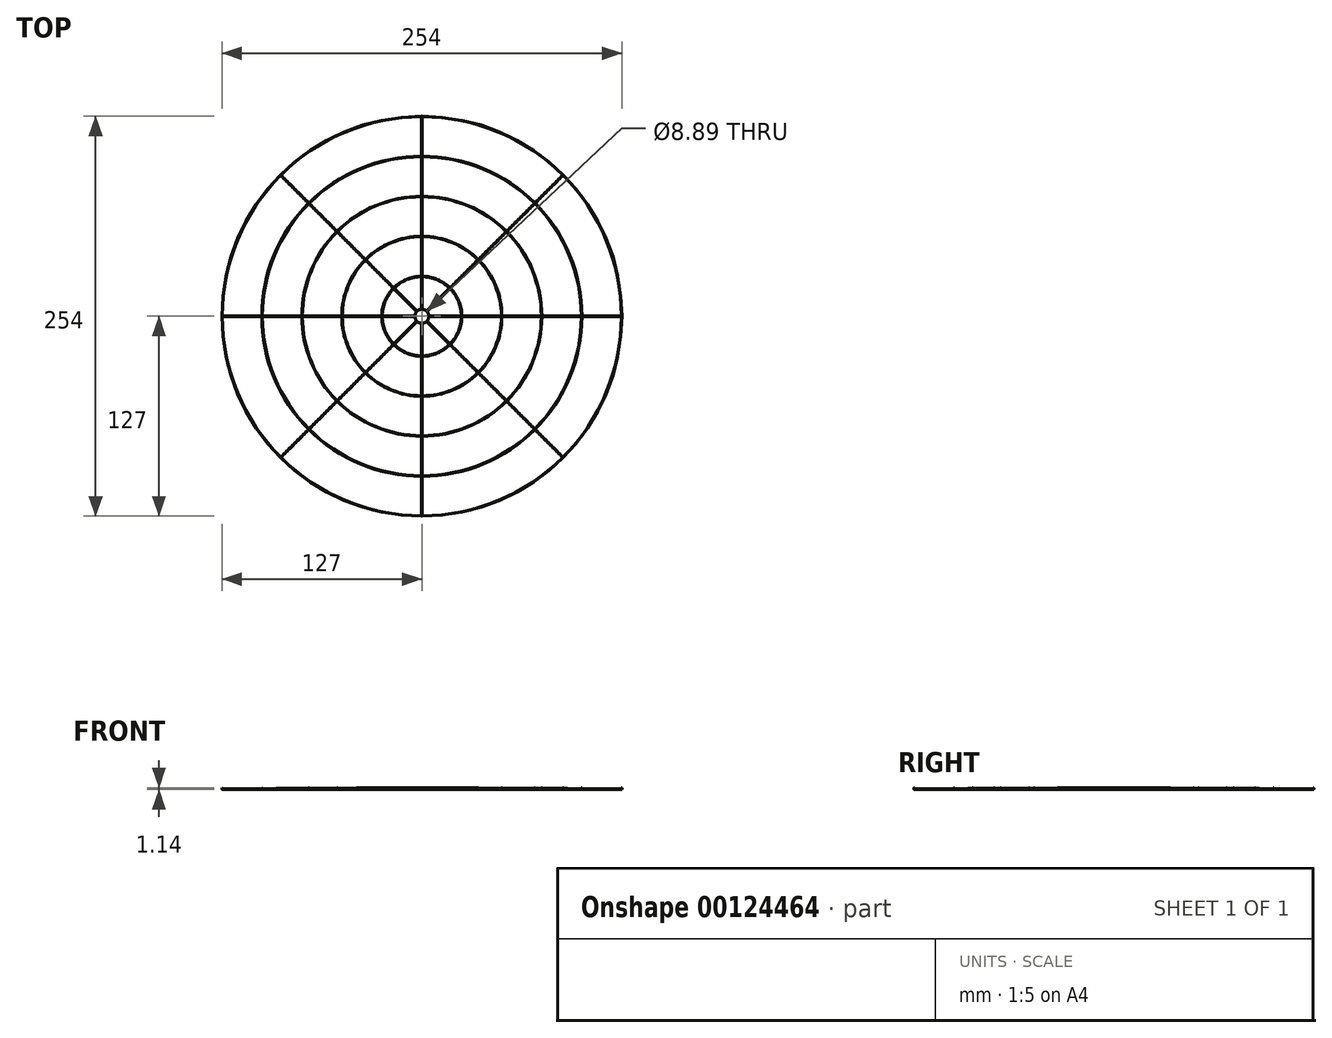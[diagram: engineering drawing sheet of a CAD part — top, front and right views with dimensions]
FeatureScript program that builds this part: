
annotation { "Feature Type Name" : "Feature", "Feature Type Description" : "" }
export const myFeature = defineFeature(function(context is Context, id is Id, definition is map)
    precondition{}
    {
        {
            var Q0;
            Q0=qCreatedBy(makeId("Front.planeOp"),FACE);
            var sketch = newSketch(context, id + "F0", { "sketchPlane" : qUnion([Q0])});
            skLineSegment(sketch, "E0", {"start": v(0, 0) * mm, "end": v(127, 0) * mm});
            skLineSegment(sketch, "E1", {"start": v(0, 0) * mm, "end": v(-127, 0) * mm});
            skLineSegment(sketch, "E2", {"start": v(-127, 0) * mm, "end": v(-127, 0.13) * mm});
            skLineSegment(sketch, "E3", {"start": v(0, 0) * mm, "end": v(0, 0.89) * mm});
            skLineSegment(sketch, "E4", {"start": v(0, 0.89) * mm, "end": v(-4.45, 0.89) * mm});
            skLineSegment(sketch, "E5", {"start": v(-4.45, 0.89) * mm, "end": v(-4.45, 0) * mm});
            skLineSegment(sketch, "E6.MirrorCS", {"start": v(0, 0.89) * mm, "end": v(4.45, 0.89) * mm});
            skLineSegment(sketch, "E7.MirrorCS", {"start": v(4.45, 0.89) * mm, "end": v(4.45, 0) * mm});
            skLineSegment(sketch, "E8.MirrorCS", {"start": v(127, 0) * mm, "end": v(127, 0.13) * mm});
            skLineSegment(sketch, "E9", {"start": v(127, 0.13) * mm, "end": v(4.45, 0.89) * mm});
            skLineSegment(sketch, "E10.MirrorCS", {"start": v(-127, 0.13) * mm, "end": v(-4.44, 0.89) * mm});
            skPoint(sketch, "E11", {"position": v(-127, 0.12) * mm});
            skPoint(sketch, "E12", {"position": v(-4.45, 0.89) * mm});
            skLineSegment(sketch, "E13", {"start": v(-4.44, 0.89) * mm, "end": v(-127, 0.12) * mm});
            skLineSegment(sketch, "E14.MirrorCS", {"start": v(4.45, 0.89) * mm, "end": v(127, 0.12) * mm});
            skSolve(sketch);
        }
        {
            var Q0;
            {var subQ0=sQuery(id+"F0.wireOp",EDGE,"E10.MirrorCS");Q0=makeQuery(id+"F0.imprint","IMPRINT",FACE,{"disambiguationData":[TD([[makeQuery(id+"F0.imprint","IMPRINT",EDGE,{"derivedFrom":subQ0}),-1.0]])]});}
            var Q1;
            Q1=sQuery(id+"F0.wireOp",EDGE,"E3");
            revolve(context, id + "F1", {"entities" : qUnion([Q0]), "axis" : qUnion([Q1]), "revolveType" : RevolveType.FULL});
        }
        {
            var Q0;
            Q0=qCreatedBy(makeId("Top.planeOp"),FACE);
            var sketch = newSketch(context, id + "F2", { "sketchPlane" : qUnion([Q0])});
            skCircle(sketch, "E15.0", {"center": v(0, 0) * mm, "radius": 127 * mm});
            skArc(sketch, "E16", {"start": v(-0.13, 76.2) * mm, "mid": v(-29.16, 70.4) * mm, "end": v(-53.8, 53.97) * mm});
            skArc(sketch, "E17", {"start": v(-0.13, 101.6) * mm, "mid": v(-38.88, 93.87) * mm, "end": v(-71.75, 71.93) * mm});
            skArc(sketch, "E18", {"start": v(-0.13, 50.8) * mm, "mid": v(-19.44, 46.93) * mm, "end": v(-35.83, 36.01) * mm});
            skArc(sketch, "E19", {"start": v(-0.13, 25.4) * mm, "mid": v(-9.72, 23.47) * mm, "end": v(-17.87, 18.05) * mm});
            skLineSegment(sketch, "E20", {"start": v(0, 0) * mm, "end": v(0, 4.45) * mm});
            skCircle(sketch, "E21.0", {"center": v(0, 0) * mm, "radius": 4.45 * mm});
            skLineSegment(sketch, "E22", {"start": v(-0.13, 5.62) * mm, "end": v(-0.13, 4.44) * mm});
            skLineSegment(sketch, "E23", {"start": v(0.13, 5.62) * mm, "end": v(0.13, 4.44) * mm});
            skLineSegment(sketch, "E24", {"start": v(-0.13, 5.62) * mm, "end": v(-0.13, 25.15) * mm});
            skLineSegment(sketch, "E25", {"start": v(0.13, 5.62) * mm, "end": v(0.13, 25.15) * mm});
            skLineSegment(sketch, "E26.1.0", {"start": v(-3.88, 4.06) * mm, "end": v(-17.7, 17.87) * mm});
            skLineSegment(sketch, "E26.1.1", {"start": v(-4.06, 3.88) * mm, "end": v(-17.87, 17.7) * mm});
            skLineSegment(sketch, "E26.1.2", {"start": v(-4.06, 3.88) * mm, "end": v(-3.23, 3.05) * mm});
            skLineSegment(sketch, "E26.1.3", {"start": v(-3.88, 4.06) * mm, "end": v(-3.05, 3.23) * mm});
            skLineSegment(sketch, "E26.2.0", {"start": v(-5.62, 0.13) * mm, "end": v(-25.15, 0.13) * mm});
            skLineSegment(sketch, "E26.2.1", {"start": v(-5.62, -0.13) * mm, "end": v(-25.15, -0.13) * mm});
            skLineSegment(sketch, "E26.2.2", {"start": v(-5.62, -0.13) * mm, "end": v(-4.44, -0.13) * mm});
            skLineSegment(sketch, "E26.2.3", {"start": v(-5.62, 0.13) * mm, "end": v(-4.44, 0.13) * mm});
            skLineSegment(sketch, "E26.3.0", {"start": v(-4.06, -3.88) * mm, "end": v(-17.87, -17.7) * mm});
            skLineSegment(sketch, "E26.3.1", {"start": v(-3.88, -4.06) * mm, "end": v(-17.7, -17.87) * mm});
            skLineSegment(sketch, "E26.3.2", {"start": v(-3.88, -4.06) * mm, "end": v(-3.05, -3.23) * mm});
            skLineSegment(sketch, "E26.3.3", {"start": v(-4.06, -3.88) * mm, "end": v(-3.23, -3.05) * mm});
            skLineSegment(sketch, "E26.4.0", {"start": v(-0.13, -5.62) * mm, "end": v(-0.13, -25.15) * mm});
            skLineSegment(sketch, "E26.4.1", {"start": v(0.13, -5.62) * mm, "end": v(0.13, -25.15) * mm});
            skLineSegment(sketch, "E26.4.2", {"start": v(0.13, -5.62) * mm, "end": v(0.13, -4.44) * mm});
            skLineSegment(sketch, "E26.4.3", {"start": v(-0.13, -5.62) * mm, "end": v(-0.13, -4.44) * mm});
            skLineSegment(sketch, "E26.5.0", {"start": v(3.88, -4.06) * mm, "end": v(17.7, -17.87) * mm});
            skLineSegment(sketch, "E26.5.1", {"start": v(4.06, -3.88) * mm, "end": v(17.87, -17.7) * mm});
            skLineSegment(sketch, "E26.5.2", {"start": v(4.06, -3.88) * mm, "end": v(3.23, -3.05) * mm});
            skLineSegment(sketch, "E26.5.3", {"start": v(3.88, -4.06) * mm, "end": v(3.05, -3.23) * mm});
            skLineSegment(sketch, "E26.6.0", {"start": v(5.62, -0.13) * mm, "end": v(25.15, -0.13) * mm});
            skLineSegment(sketch, "E26.6.1", {"start": v(5.62, 0.13) * mm, "end": v(25.15, 0.13) * mm});
            skLineSegment(sketch, "E26.6.2", {"start": v(5.62, 0.13) * mm, "end": v(4.44, 0.13) * mm});
            skLineSegment(sketch, "E26.6.3", {"start": v(5.62, -0.13) * mm, "end": v(4.44, -0.13) * mm});
            skLineSegment(sketch, "E26.7.0", {"start": v(4.06, 3.88) * mm, "end": v(17.87, 17.7) * mm});
            skLineSegment(sketch, "E26.7.1", {"start": v(3.88, 4.06) * mm, "end": v(17.7, 17.87) * mm});
            skLineSegment(sketch, "E26.7.2", {"start": v(3.88, 4.06) * mm, "end": v(3.05, 3.23) * mm});
            skLineSegment(sketch, "E26.7.3", {"start": v(4.06, 3.88) * mm, "end": v(3.23, 3.05) * mm});
            skArc(sketch, "E27.trimOffspring", {"start": v(17.87, 18.05) * mm, "mid": v(9.72, 23.47) * mm, "end": v(0.13, 25.4) * mm});
            skArc(sketch, "E28.trimOffspring", {"start": v(35.83, 36.01) * mm, "mid": v(19.44, 46.93) * mm, "end": v(0.13, 50.8) * mm});
            skArc(sketch, "E29.trimOffspring", {"start": v(53.8, 53.97) * mm, "mid": v(29.16, 70.4) * mm, "end": v(0.13, 76.2) * mm});
            skArc(sketch, "E30.trimOffspring", {"start": v(71.75, 71.93) * mm, "mid": v(38.88, 93.87) * mm, "end": v(0.13, 101.6) * mm});
            skArc(sketch, "E31.trimOffspring", {"start": v(101.6, 0.13) * mm, "mid": v(93.87, 38.88) * mm, "end": v(71.93, 71.75) * mm});
            skArc(sketch, "E32.trimOffspring", {"start": v(76.2, 0.13) * mm, "mid": v(70.4, 29.16) * mm, "end": v(53.97, 53.8) * mm});
            skArc(sketch, "E33.trimOffspring", {"start": v(50.8, 0.13) * mm, "mid": v(46.93, 19.44) * mm, "end": v(36.01, 35.83) * mm});
            skArc(sketch, "E34.trimOffspring", {"start": v(25.4, 0.13) * mm, "mid": v(23.47, 9.72) * mm, "end": v(18.05, 17.87) * mm});
            skArc(sketch, "E35.trimOffspring", {"start": v(18.05, -17.87) * mm, "mid": v(23.47, -9.72) * mm, "end": v(25.4, -0.13) * mm});
            skArc(sketch, "E36.trimOffspring", {"start": v(36.01, -35.83) * mm, "mid": v(46.93, -19.44) * mm, "end": v(50.8, -0.13) * mm});
            skArc(sketch, "E37.trimOffspring", {"start": v(53.97, -53.8) * mm, "mid": v(70.4, -29.16) * mm, "end": v(76.2, -0.13) * mm});
            skArc(sketch, "E38.trimOffspring", {"start": v(71.93, -71.75) * mm, "mid": v(93.87, -38.88) * mm, "end": v(101.6, -0.13) * mm});
            skArc(sketch, "E39.trimOffspring", {"start": v(0.13, -101.6) * mm, "mid": v(38.88, -93.87) * mm, "end": v(71.75, -71.93) * mm});
            skArc(sketch, "E40.trimOffspring", {"start": v(0.13, -76.2) * mm, "mid": v(29.16, -70.4) * mm, "end": v(53.8, -53.97) * mm});
            skArc(sketch, "E41.trimOffspring", {"start": v(0.13, -50.8) * mm, "mid": v(19.44, -46.93) * mm, "end": v(35.83, -36.01) * mm});
            skArc(sketch, "E42.trimOffspring", {"start": v(0.13, -25.4) * mm, "mid": v(9.72, -23.47) * mm, "end": v(17.87, -18.05) * mm});
            skArc(sketch, "E43.trimOffspring", {"start": v(-17.87, -18.05) * mm, "mid": v(-9.72, -23.47) * mm, "end": v(-0.13, -25.4) * mm});
            skArc(sketch, "E44.trimOffspring", {"start": v(-35.83, -36.01) * mm, "mid": v(-19.44, -46.93) * mm, "end": v(-0.13, -50.8) * mm});
            skArc(sketch, "E45.trimOffspring", {"start": v(-53.8, -53.97) * mm, "mid": v(-29.16, -70.4) * mm, "end": v(-0.13, -76.2) * mm});
            skArc(sketch, "E46.trimOffspring", {"start": v(-71.75, -71.93) * mm, "mid": v(-38.88, -93.87) * mm, "end": v(-0.13, -101.6) * mm});
            skArc(sketch, "E47.trimOffspring", {"start": v(-50.8, -0.13) * mm, "mid": v(-46.93, -19.44) * mm, "end": v(-36.01, -35.83) * mm});
            skArc(sketch, "E48.trimOffspring", {"start": v(-25.4, -0.13) * mm, "mid": v(-23.47, -9.72) * mm, "end": v(-18.05, -17.87) * mm});
            skArc(sketch, "E49.trimOffspring", {"start": v(-76.2, -0.13) * mm, "mid": v(-70.4, -29.16) * mm, "end": v(-53.97, -53.8) * mm});
            skArc(sketch, "E50.trimOffspring", {"start": v(-101.6, -0.13) * mm, "mid": v(-93.87, -38.88) * mm, "end": v(-71.93, -71.75) * mm});
            skArc(sketch, "E51.trimOffspring", {"start": v(-18.05, 17.87) * mm, "mid": v(-23.47, 9.72) * mm, "end": v(-25.4, 0.13) * mm});
            skArc(sketch, "E52.trimOffspring", {"start": v(-36.01, 35.83) * mm, "mid": v(-46.93, 19.44) * mm, "end": v(-50.8, 0.13) * mm});
            skArc(sketch, "E53.trimOffspring", {"start": v(-53.97, 53.8) * mm, "mid": v(-70.4, 29.16) * mm, "end": v(-76.2, 0.13) * mm});
            skArc(sketch, "E54.trimOffspring", {"start": v(-71.93, 71.75) * mm, "mid": v(-93.87, 38.88) * mm, "end": v(-101.6, 0.13) * mm});
            skArc(sketch, "E55", {"start": v(-89.71, 89.53) * mm, "mid": v(-117.1, 48.5) * mm, "end": v(-126.75, 0.13) * mm});
            skArc(sketch, "E56.trimOffspring", {"start": v(-0.13, 126.75) * mm, "mid": v(-48.5, 117.1) * mm, "end": v(-89.53, 89.71) * mm});
            skArc(sketch, "E57.trimOffspring", {"start": v(89.53, 89.71) * mm, "mid": v(48.5, 117.1) * mm, "end": v(0.13, 126.75) * mm});
            skArc(sketch, "E58.trimOffspring", {"start": v(126.75, 0.13) * mm, "mid": v(117.1, 48.5) * mm, "end": v(89.71, 89.53) * mm});
            skArc(sketch, "E59.trimOffspring", {"start": v(89.71, -89.53) * mm, "mid": v(117.1, -48.5) * mm, "end": v(126.75, -0.13) * mm});
            skArc(sketch, "E60.trimOffspring", {"start": v(0.13, -126.75) * mm, "mid": v(48.5, -117.1) * mm, "end": v(89.53, -89.71) * mm});
            skArc(sketch, "E61.trimOffspring", {"start": v(-89.53, -89.71) * mm, "mid": v(-48.5, -117.1) * mm, "end": v(-0.13, -126.75) * mm});
            skArc(sketch, "E62.trimOffspring", {"start": v(-126.75, -0.13) * mm, "mid": v(-117.1, -48.5) * mm, "end": v(-89.71, -89.53) * mm});
            skPoint(sketch, "E63.orphan", {"position": v(-89.9, 89.71) * mm});
            skPoint(sketch, "E64.orphan", {"position": v(-89.71, 89.9) * mm});
            skPoint(sketch, "E65.orphan", {"position": v(-0.13, 127) * mm});
            skPoint(sketch, "E66.orphan", {"position": v(0.13, 127) * mm});
            skPoint(sketch, "E67.orphan", {"position": v(89.71, 89.9) * mm});
            skPoint(sketch, "E68.orphan", {"position": v(89.9, 89.71) * mm});
            skPoint(sketch, "E69.orphan", {"position": v(127, 0.13) * mm});
            skPoint(sketch, "E70.orphan", {"position": v(127, -0.13) * mm});
            skPoint(sketch, "E71.orphan", {"position": v(89.71, -89.9) * mm});
            skPoint(sketch, "E72.orphan", {"position": v(89.9, -89.71) * mm});
            skPoint(sketch, "E73.orphan", {"position": v(-0.13, -127) * mm});
            skPoint(sketch, "E74.orphan", {"position": v(0.13, -127) * mm});
            skPoint(sketch, "E75.orphan", {"position": v(-89.9, -89.71) * mm});
            skPoint(sketch, "E76.orphan", {"position": v(-89.71, -89.9) * mm});
            skPoint(sketch, "E77.orphan", {"position": v(-127, 0.13) * mm});
            skPoint(sketch, "E78.orphan", {"position": v(-127, -0.13) * mm});
            skArc(sketch, "E79", {"start": v(-0.13, 101.35) * mm, "mid": v(-38.78, 93.63) * mm, "end": v(-71.57, 71.75) * mm});
            skLineSegment(sketch, "E80.trimOffspring", {"start": v(-0.13, 101.6) * mm, "end": v(-0.13, 126.75) * mm});
            skLineSegment(sketch, "E81.trimOffspring", {"start": v(0.13, 101.6) * mm, "end": v(0.13, 126.75) * mm});
            skArc(sketch, "E82.trimOffspring", {"start": v(71.57, 71.75) * mm, "mid": v(38.78, 93.63) * mm, "end": v(0.13, 101.35) * mm});
            skLineSegment(sketch, "E83.trimOffspring", {"start": v(71.75, 71.93) * mm, "end": v(89.53, 89.71) * mm});
            skLineSegment(sketch, "E84.trimOffspring", {"start": v(71.93, 71.75) * mm, "end": v(89.71, 89.53) * mm});
            skLineSegment(sketch, "E85.trimOffspring", {"start": v(101.6, 0.13) * mm, "end": v(126.75, 0.13) * mm});
            skArc(sketch, "E86.trimOffspring", {"start": v(101.35, 0.13) * mm, "mid": v(93.63, 38.78) * mm, "end": v(71.75, 71.57) * mm});
            skLineSegment(sketch, "E87.trimOffspring", {"start": v(101.6, -0.13) * mm, "end": v(126.75, -0.13) * mm});
            skLineSegment(sketch, "E88.trimOffspring", {"start": v(71.93, -71.75) * mm, "end": v(89.71, -89.53) * mm});
            skArc(sketch, "E89.trimOffspring", {"start": v(71.75, -71.57) * mm, "mid": v(93.63, -38.78) * mm, "end": v(101.35, -0.13) * mm});
            skLineSegment(sketch, "E90.trimOffspring", {"start": v(71.75, -71.93) * mm, "end": v(89.53, -89.71) * mm});
            skLineSegment(sketch, "E91.trimOffspring", {"start": v(0.13, -101.6) * mm, "end": v(0.13, -126.75) * mm});
            skLineSegment(sketch, "E92.trimOffspring", {"start": v(-0.13, -101.6) * mm, "end": v(-0.13, -126.75) * mm});
            skArc(sketch, "E93.trimOffspring", {"start": v(0.13, -101.35) * mm, "mid": v(38.78, -93.63) * mm, "end": v(71.57, -71.75) * mm});
            skLineSegment(sketch, "E94.trimOffspring", {"start": v(-71.93, -71.75) * mm, "end": v(-89.71, -89.53) * mm});
            skArc(sketch, "E95.trimOffspring", {"start": v(-71.57, -71.75) * mm, "mid": v(-38.78, -93.63) * mm, "end": v(-0.13, -101.35) * mm});
            skLineSegment(sketch, "E96.trimOffspring", {"start": v(-71.75, -71.93) * mm, "end": v(-89.53, -89.71) * mm});
            skArc(sketch, "E97.trimOffspring", {"start": v(-101.35, -0.13) * mm, "mid": v(-93.63, -38.78) * mm, "end": v(-71.75, -71.57) * mm});
            skLineSegment(sketch, "E98.trimOffspring", {"start": v(-101.6, 0.13) * mm, "end": v(-126.75, 0.13) * mm});
            skLineSegment(sketch, "E99.trimOffspring", {"start": v(-101.6, -0.13) * mm, "end": v(-126.75, -0.13) * mm});
            skLineSegment(sketch, "E100.trimOffspring", {"start": v(-71.75, 71.93) * mm, "end": v(-89.53, 89.71) * mm});
            skLineSegment(sketch, "E101.trimOffspring", {"start": v(-71.93, 71.75) * mm, "end": v(-89.71, 89.53) * mm});
            skArc(sketch, "E102.trimOffspring", {"start": v(-71.75, 71.57) * mm, "mid": v(-93.63, 38.78) * mm, "end": v(-101.35, 0.13) * mm});
            skArc(sketch, "E103", {"start": v(-0.13, 75.95) * mm, "mid": v(-29.06, 70.16) * mm, "end": v(-53.61, 53.8) * mm});
            skLineSegment(sketch, "E104.trimOffspring", {"start": v(-0.13, 76.2) * mm, "end": v(-0.13, 101.35) * mm});
            skLineSegment(sketch, "E105.trimOffspring", {"start": v(0.13, 76.2) * mm, "end": v(0.13, 101.35) * mm});
            skArc(sketch, "E106.trimOffspring", {"start": v(53.61, 53.8) * mm, "mid": v(29.06, 70.16) * mm, "end": v(0.13, 75.95) * mm});
            skLineSegment(sketch, "E107.trimOffspring", {"start": v(53.8, 53.97) * mm, "end": v(71.57, 71.75) * mm});
            skLineSegment(sketch, "E108.trimOffspring", {"start": v(53.97, 53.8) * mm, "end": v(71.75, 71.57) * mm});
            skArc(sketch, "E109.trimOffspring", {"start": v(75.95, 0.13) * mm, "mid": v(70.16, 29.06) * mm, "end": v(53.8, 53.61) * mm});
            skLineSegment(sketch, "E110.trimOffspring", {"start": v(76.2, 0.13) * mm, "end": v(101.35, 0.13) * mm});
            skLineSegment(sketch, "E111.trimOffspring", {"start": v(76.2, -0.13) * mm, "end": v(101.35, -0.13) * mm});
            skArc(sketch, "E112.trimOffspring", {"start": v(53.8, -53.61) * mm, "mid": v(70.16, -29.06) * mm, "end": v(75.95, -0.13) * mm});
            skLineSegment(sketch, "E113.trimOffspring", {"start": v(53.97, -53.8) * mm, "end": v(71.75, -71.57) * mm});
            skLineSegment(sketch, "E114.trimOffspring", {"start": v(53.8, -53.97) * mm, "end": v(71.57, -71.75) * mm});
            skArc(sketch, "E115.trimOffspring", {"start": v(0.13, -75.95) * mm, "mid": v(29.06, -70.16) * mm, "end": v(53.61, -53.8) * mm});
            skLineSegment(sketch, "E116.trimOffspring", {"start": v(-0.13, -76.2) * mm, "end": v(-0.13, -101.35) * mm});
            skLineSegment(sketch, "E117.trimOffspring", {"start": v(0.13, -76.2) * mm, "end": v(0.13, -101.35) * mm});
            skArc(sketch, "E118.trimOffspring", {"start": v(-53.61, -53.8) * mm, "mid": v(-29.06, -70.16) * mm, "end": v(-0.13, -75.95) * mm});
            skLineSegment(sketch, "E119.trimOffspring", {"start": v(-53.97, -53.8) * mm, "end": v(-71.75, -71.57) * mm});
            skLineSegment(sketch, "E120.trimOffspring", {"start": v(-53.8, -53.97) * mm, "end": v(-71.57, -71.75) * mm});
            skLineSegment(sketch, "E121.trimOffspring", {"start": v(-76.2, 0.13) * mm, "end": v(-101.35, 0.13) * mm});
            skLineSegment(sketch, "E122.trimOffspring", {"start": v(-76.2, -0.13) * mm, "end": v(-101.35, -0.13) * mm});
            skArc(sketch, "E123.trimOffspring", {"start": v(-75.95, -0.13) * mm, "mid": v(-70.16, -29.06) * mm, "end": v(-53.8, -53.61) * mm});
            skLineSegment(sketch, "E124.trimOffspring", {"start": v(-53.97, 53.8) * mm, "end": v(-71.75, 71.57) * mm});
            skArc(sketch, "E125.trimOffspring", {"start": v(-53.8, 53.61) * mm, "mid": v(-70.16, 29.06) * mm, "end": v(-75.95, 0.13) * mm});
            skLineSegment(sketch, "E126.trimOffspring", {"start": v(-53.8, 53.97) * mm, "end": v(-71.57, 71.75) * mm});
            skArc(sketch, "E127", {"start": v(-0.13, 50.55) * mm, "mid": v(-19.34, 46.7) * mm, "end": v(-35.65, 35.83) * mm});
            skLineSegment(sketch, "E128.trimOffspring", {"start": v(-0.13, 50.8) * mm, "end": v(-0.13, 75.95) * mm});
            skLineSegment(sketch, "E129.trimOffspring", {"start": v(0.13, 50.8) * mm, "end": v(0.13, 75.95) * mm});
            skLineSegment(sketch, "E130.trimOffspring", {"start": v(35.83, 36.01) * mm, "end": v(53.61, 53.8) * mm});
            skArc(sketch, "E131.trimOffspring", {"start": v(35.65, 35.83) * mm, "mid": v(19.34, 46.7) * mm, "end": v(0.13, 50.55) * mm});
            skLineSegment(sketch, "E132.trimOffspring", {"start": v(36.01, 35.83) * mm, "end": v(53.8, 53.61) * mm});
            skLineSegment(sketch, "E133.trimOffspring", {"start": v(50.8, 0.13) * mm, "end": v(75.95, 0.13) * mm});
            skLineSegment(sketch, "E134.trimOffspring", {"start": v(50.8, -0.13) * mm, "end": v(75.95, -0.13) * mm});
            skArc(sketch, "E135.trimOffspring", {"start": v(50.55, 0.13) * mm, "mid": v(46.7, 19.34) * mm, "end": v(35.83, 35.65) * mm});
            skArc(sketch, "E136.trimOffspring", {"start": v(35.83, -35.65) * mm, "mid": v(46.7, -19.34) * mm, "end": v(50.55, -0.13) * mm});
            skLineSegment(sketch, "E137.trimOffspring", {"start": v(36.01, -35.83) * mm, "end": v(53.8, -53.61) * mm});
            skLineSegment(sketch, "E138.trimOffspring", {"start": v(35.83, -36.01) * mm, "end": v(53.61, -53.8) * mm});
            skArc(sketch, "E139.trimOffspring", {"start": v(0.13, -50.55) * mm, "mid": v(19.34, -46.7) * mm, "end": v(35.65, -35.83) * mm});
            skLineSegment(sketch, "E140.trimOffspring", {"start": v(-0.13, -50.8) * mm, "end": v(-0.13, -75.95) * mm});
            skLineSegment(sketch, "E141.trimOffspring", {"start": v(0.13, -50.8) * mm, "end": v(0.13, -75.95) * mm});
            skLineSegment(sketch, "E142.trimOffspring", {"start": v(-36.01, -35.83) * mm, "end": v(-53.8, -53.61) * mm});
            skArc(sketch, "E143.trimOffspring", {"start": v(-35.65, -35.83) * mm, "mid": v(-19.34, -46.7) * mm, "end": v(-0.13, -50.55) * mm});
            skLineSegment(sketch, "E144.trimOffspring", {"start": v(-35.83, -36.01) * mm, "end": v(-53.61, -53.8) * mm});
            skLineSegment(sketch, "E145.trimOffspring", {"start": v(-50.8, 0.13) * mm, "end": v(-75.95, 0.13) * mm});
            skLineSegment(sketch, "E146.trimOffspring", {"start": v(-50.8, -0.13) * mm, "end": v(-75.95, -0.13) * mm});
            skLineSegment(sketch, "E147.trimOffspring", {"start": v(-35.83, 36.01) * mm, "end": v(-53.61, 53.8) * mm});
            skLineSegment(sketch, "E148.trimOffspring", {"start": v(-36.01, 35.83) * mm, "end": v(-53.8, 53.61) * mm});
            skArc(sketch, "E149.trimOffspring", {"start": v(-35.83, 35.65) * mm, "mid": v(-50.55, 0) * mm, "end": v(-35.83, -35.65) * mm});
            skArc(sketch, "E150", {"start": v(-0.13, 25.15) * mm, "mid": v(-9.62, 23.23) * mm, "end": v(-17.7, 17.87) * mm});
            skLineSegment(sketch, "E151.trimOffspring", {"start": v(-0.13, 25.4) * mm, "end": v(-0.13, 50.55) * mm});
            skLineSegment(sketch, "E152.trimOffspring", {"start": v(0.13, 25.4) * mm, "end": v(0.13, 50.55) * mm});
            skLineSegment(sketch, "E153.trimOffspring", {"start": v(17.87, 18.05) * mm, "end": v(35.65, 35.83) * mm});
            skArc(sketch, "E154.trimOffspring", {"start": v(17.7, 17.87) * mm, "mid": v(9.62, 23.23) * mm, "end": v(0.13, 25.15) * mm});
            skLineSegment(sketch, "E155.trimOffspring", {"start": v(18.05, 17.87) * mm, "end": v(35.83, 35.65) * mm});
            skLineSegment(sketch, "E156.trimOffspring", {"start": v(25.4, -0.13) * mm, "end": v(50.55, -0.13) * mm});
            skArc(sketch, "E157.trimOffspring", {"start": v(25.15, 0.13) * mm, "mid": v(23.23, 9.62) * mm, "end": v(17.87, 17.7) * mm});
            skLineSegment(sketch, "E158.trimOffspring", {"start": v(25.4, 0.13) * mm, "end": v(50.55, 0.13) * mm});
            skLineSegment(sketch, "E159.trimOffspring", {"start": v(17.87, -18.05) * mm, "end": v(35.65, -35.83) * mm});
            skArc(sketch, "E160.trimOffspring", {"start": v(17.87, -17.7) * mm, "mid": v(23.23, -9.62) * mm, "end": v(25.15, -0.13) * mm});
            skLineSegment(sketch, "E161.trimOffspring", {"start": v(18.05, -17.87) * mm, "end": v(35.83, -35.65) * mm});
            skArc(sketch, "E162.trimOffspring", {"start": v(0.13, -25.15) * mm, "mid": v(9.62, -23.23) * mm, "end": v(17.7, -17.87) * mm});
            skLineSegment(sketch, "E163.trimOffspring", {"start": v(-0.13, -25.4) * mm, "end": v(-0.13, -50.55) * mm});
            skLineSegment(sketch, "E164.trimOffspring", {"start": v(0.13, -25.4) * mm, "end": v(0.13, -50.55) * mm});
            skLineSegment(sketch, "E165.trimOffspring", {"start": v(-18.05, -17.87) * mm, "end": v(-35.83, -35.65) * mm});
            skLineSegment(sketch, "E166.trimOffspring", {"start": v(-17.87, -18.05) * mm, "end": v(-35.65, -35.83) * mm});
            skArc(sketch, "E167.trimOffspring", {"start": v(-17.7, -17.87) * mm, "mid": v(-9.62, -23.23) * mm, "end": v(-0.13, -25.15) * mm});
            skArc(sketch, "E168.trimOffspring", {"start": v(-25.15, -0.13) * mm, "mid": v(-23.23, -9.62) * mm, "end": v(-17.87, -17.7) * mm});
            skLineSegment(sketch, "E169.trimOffspring", {"start": v(-25.4, 0.13) * mm, "end": v(-50.55, 0.13) * mm});
            skLineSegment(sketch, "E170.trimOffspring", {"start": v(-25.4, -0.13) * mm, "end": v(-50.55, -0.13) * mm});
            skArc(sketch, "E171.trimOffspring", {"start": v(-17.87, 17.7) * mm, "mid": v(-23.23, 9.62) * mm, "end": v(-25.15, 0.13) * mm});
            skLineSegment(sketch, "E172.trimOffspring", {"start": v(-18.05, 17.87) * mm, "end": v(-35.83, 35.65) * mm});
            skLineSegment(sketch, "E173.trimOffspring", {"start": v(-17.87, 18.05) * mm, "end": v(-35.65, 35.83) * mm});
            skSolve(sketch);
        }
        {
            var Q0;
            Q0=makeQuery(id+"F2.imprint","IMPRINT",FACE,{"disambiguationData":[TD([[makeQuery(id+"F2.imprint","IMPRINT",EDGE,{"derivedFrom":sQuery(id+"F2.wireOp",EDGE,"E15.0")}),1.0]])]});
            extrude(context, id + "F3", {"entities" : qUnion([Q0]), "operationType" : NewBodyOperationType.REMOVE, "depth" : 25.4 * mm});
        }
        {
            var Q0;
            {var subQ0=sQuery(id+"F0.wireOp",EDGE,"E10.MirrorCS");Q0=makeQuery(id+"F0.imprint","IMPRINT",FACE,{"disambiguationData":[TD([[makeQuery(id+"F0.imprint","IMPRINT",EDGE,{"derivedFrom":subQ0}),-1.0]])]});}
            var Q1;
            Q1=sQuery(id+"F0.wireOp",EDGE,"E3");
            revolve(context, id + "F4", {"entities" : qUnion([Q0]), "axis" : qUnion([Q1]), "revolveType" : RevolveType.FULL});
        }
        {
            var Q0;
            Q0=makeQuery(id+"F2.imprint","IMPRINT",FACE,{"disambiguationData":[TD([[makeQuery(id+"F2.imprint","IMPRINT",EDGE,{"derivedFrom":sQuery(id+"F2.wireOp",EDGE,"E46.trimOffspring")}),-1.0]])]});
            var Q1;
            Q1=makeQuery(id+"F2.imprint","IMPRINT",FACE,{"disambiguationData":[TD([[makeQuery(id+"F2.imprint","IMPRINT",EDGE,{"derivedFrom":sQuery(id+"F2.wireOp",EDGE,"E45.trimOffspring")}),-1.0]])]});
            var Q2;
            Q2=makeQuery(id+"F2.imprint","IMPRINT",FACE,{"disambiguationData":[TD([[makeQuery(id+"F2.imprint","IMPRINT",EDGE,{"derivedFrom":sQuery(id+"F2.wireOp",EDGE,"E50.trimOffspring")}),-1.0]])]});
            var Q3;
            Q3=makeQuery(id+"F2.imprint","IMPRINT",FACE,{"disambiguationData":[TD([[makeQuery(id+"F2.imprint","IMPRINT",EDGE,{"derivedFrom":sQuery(id+"F2.wireOp",EDGE,"E49.trimOffspring")}),-1.0]])]});
            var Q4;
            Q4=makeQuery(id+"F2.imprint","IMPRINT",FACE,{"disambiguationData":[TD([[makeQuery(id+"F2.imprint","IMPRINT",EDGE,{"derivedFrom":sQuery(id+"F2.wireOp",EDGE,"E54.trimOffspring")}),-1.0]])]});
            var Q5;
            Q5=makeQuery(id+"F2.imprint","IMPRINT",FACE,{"disambiguationData":[TD([[makeQuery(id+"F2.imprint","IMPRINT",EDGE,{"derivedFrom":sQuery(id+"F2.wireOp",EDGE,"E53.trimOffspring")}),-1.0]])]});
            var Q6;
            Q6=makeQuery(id+"F2.imprint","IMPRINT",FACE,{"disambiguationData":[TD([[makeQuery(id+"F2.imprint","IMPRINT",EDGE,{"derivedFrom":sQuery(id+"F2.wireOp",EDGE,"E52.trimOffspring")}),-1.0]])]});
            var Q7;
            Q7=makeQuery(id+"F2.imprint","IMPRINT",FACE,{"disambiguationData":[TD([[makeQuery(id+"F2.imprint","IMPRINT",EDGE,{"derivedFrom":sQuery(id+"F2.wireOp",EDGE,"E48.trimOffspring")}),-1.0]])]});
            var Q8;
            Q8=makeQuery(id+"F2.imprint","IMPRINT",FACE,{"disambiguationData":[TD([[makeQuery(id+"F2.imprint","IMPRINT",EDGE,{"derivedFrom":sQuery(id+"F2.wireOp",EDGE,"E44.trimOffspring")}),-1.0]])]});
            var Q9;
            Q9=makeQuery(id+"F2.imprint","IMPRINT",FACE,{"disambiguationData":[TD([[makeQuery(id+"F2.imprint","IMPRINT",EDGE,{"derivedFrom":sQuery(id+"F2.wireOp",EDGE,"E41.trimOffspring")}),-1.0]])]});
            var Q10;
            Q10=makeQuery(id+"F2.imprint","IMPRINT",FACE,{"disambiguationData":[TD([[makeQuery(id+"F2.imprint","IMPRINT",EDGE,{"derivedFrom":sQuery(id+"F2.wireOp",EDGE,"E40.trimOffspring")}),-1.0]])]});
            var Q11;
            Q11=makeQuery(id+"F2.imprint","IMPRINT",FACE,{"disambiguationData":[TD([[makeQuery(id+"F2.imprint","IMPRINT",EDGE,{"derivedFrom":sQuery(id+"F2.wireOp",EDGE,"E39.trimOffspring")}),-1.0]])]});
            var Q12;
            Q12=makeQuery(id+"F2.imprint","IMPRINT",FACE,{"disambiguationData":[TD([[makeQuery(id+"F2.imprint","IMPRINT",EDGE,{"derivedFrom":sQuery(id+"F2.wireOp",EDGE,"E38.trimOffspring")}),-1.0]])]});
            var Q13;
            Q13=makeQuery(id+"F2.imprint","IMPRINT",FACE,{"disambiguationData":[TD([[makeQuery(id+"F2.imprint","IMPRINT",EDGE,{"derivedFrom":sQuery(id+"F2.wireOp",EDGE,"E37.trimOffspring")}),-1.0]])]});
            var Q14;
            Q14=makeQuery(id+"F2.imprint","IMPRINT",FACE,{"disambiguationData":[TD([[makeQuery(id+"F2.imprint","IMPRINT",EDGE,{"derivedFrom":sQuery(id+"F2.wireOp",EDGE,"E36.trimOffspring")}),-1.0]])]});
            var Q15;
            Q15=makeQuery(id+"F2.imprint","IMPRINT",FACE,{"disambiguationData":[TD([[makeQuery(id+"F2.imprint","IMPRINT",EDGE,{"derivedFrom":sQuery(id+"F2.wireOp",EDGE,"E35.trimOffspring")}),-1.0]])]});
            var Q16;
            Q16=makeQuery(id+"F2.imprint","IMPRINT",FACE,{"disambiguationData":[TD([[makeQuery(id+"F2.imprint","IMPRINT",EDGE,{"derivedFrom":sQuery(id+"F2.wireOp",EDGE,"E42.trimOffspring")}),-1.0]])]});
            var Q17;
            Q17=makeQuery(id+"F2.imprint","IMPRINT",FACE,{"disambiguationData":[TD([[makeQuery(id+"F2.imprint","IMPRINT",EDGE,{"derivedFrom":sQuery(id+"F2.wireOp",EDGE,"E43.trimOffspring")}),-1.0]])]});
            var Q18;
            Q18=makeQuery(id+"F2.imprint","IMPRINT",FACE,{"disambiguationData":[TD([[makeQuery(id+"F2.imprint","IMPRINT",EDGE,{"derivedFrom":sQuery(id+"F2.wireOp",EDGE,"E47.trimOffspring")}),-1.0]])]});
            var Q19;
            Q19=makeQuery(id+"F2.imprint","IMPRINT",FACE,{"disambiguationData":[TD([[makeQuery(id+"F2.imprint","IMPRINT",EDGE,{"derivedFrom":sQuery(id+"F2.wireOp",EDGE,"E51.trimOffspring")}),-1.0]])]});
            var Q20;
            Q20=makeQuery(id+"F2.imprint","IMPRINT",FACE,{"disambiguationData":[TD([[makeQuery(id+"F2.imprint","IMPRINT",EDGE,{"derivedFrom":sQuery(id+"F2.wireOp",EDGE,"E27.trimOffspring")}),-1.0]])]});
            var Q21;
            Q21=makeQuery(id+"F2.imprint","IMPRINT",FACE,{"disambiguationData":[TD([[makeQuery(id+"F2.imprint","IMPRINT",EDGE,{"derivedFrom":sQuery(id+"F2.wireOp",EDGE,"E34.trimOffspring")}),-1.0]])]});
            var Q22;
            Q22=makeQuery(id+"F2.imprint","IMPRINT",FACE,{"disambiguationData":[TD([[makeQuery(id+"F2.imprint","IMPRINT",EDGE,{"derivedFrom":sQuery(id+"F2.wireOp",EDGE,"E33.trimOffspring")}),-1.0]])]});
            var Q23;
            Q23=makeQuery(id+"F2.imprint","IMPRINT",FACE,{"disambiguationData":[TD([[makeQuery(id+"F2.imprint","IMPRINT",EDGE,{"derivedFrom":sQuery(id+"F2.wireOp",EDGE,"E32.trimOffspring")}),-1.0]])]});
            var Q24;
            Q24=makeQuery(id+"F2.imprint","IMPRINT",FACE,{"disambiguationData":[TD([[makeQuery(id+"F2.imprint","IMPRINT",EDGE,{"derivedFrom":sQuery(id+"F2.wireOp",EDGE,"E31.trimOffspring")}),-1.0]])]});
            var Q25;
            Q25=makeQuery(id+"F2.imprint","IMPRINT",FACE,{"disambiguationData":[TD([[makeQuery(id+"F2.imprint","IMPRINT",EDGE,{"derivedFrom":sQuery(id+"F2.wireOp",EDGE,"E30.trimOffspring")}),-1.0]])]});
            var Q26;
            Q26=makeQuery(id+"F2.imprint","IMPRINT",FACE,{"disambiguationData":[TD([[makeQuery(id+"F2.imprint","IMPRINT",EDGE,{"derivedFrom":sQuery(id+"F2.wireOp",EDGE,"E29.trimOffspring")}),-1.0]])]});
            var Q27;
            Q27=makeQuery(id+"F2.imprint","IMPRINT",FACE,{"disambiguationData":[TD([[makeQuery(id+"F2.imprint","IMPRINT",EDGE,{"derivedFrom":sQuery(id+"F2.wireOp",EDGE,"E28.trimOffspring")}),-1.0]])]});
            var Q28;
            Q28=makeQuery(id+"F2.imprint","IMPRINT",FACE,{"disambiguationData":[TD([[makeQuery(id+"F2.imprint","IMPRINT",EDGE,{"derivedFrom":sQuery(id+"F2.wireOp",EDGE,"E18")}),-1.0]])]});
            var Q29;
            Q29=makeQuery(id+"F2.imprint","IMPRINT",FACE,{"disambiguationData":[TD([[makeQuery(id+"F2.imprint","IMPRINT",EDGE,{"derivedFrom":sQuery(id+"F2.wireOp",EDGE,"E16")}),-1.0]])]});
            var Q30;
            Q30=makeQuery(id+"F2.imprint","IMPRINT",FACE,{"disambiguationData":[TD([[makeQuery(id+"F2.imprint","IMPRINT",EDGE,{"derivedFrom":sQuery(id+"F2.wireOp",EDGE,"E17")}),-1.0]])]});
            var Q31;
            Q31=makeQuery(id+"F2.imprint","IMPRINT",FACE,{"disambiguationData":[TD([[makeQuery(id+"F2.imprint","IMPRINT",EDGE,{"derivedFrom":sQuery(id+"F2.wireOp",EDGE,"E19")}),-1.0]])]});
            var Q32;
            Q32=makeQuery(id+"F2.imprint","IMPRINT",FACE,{"disambiguationData":[TD([[makeQuery(id+"F2.imprint","IMPRINT",EDGE,{"derivedFrom":sQuery(id+"F2.wireOp",EDGE,"E26.3.1")}),1.0]])]});
            var Q33;
            Q33=makeQuery(id+"F2.imprint","IMPRINT",FACE,{"disambiguationData":[TD([[makeQuery(id+"F2.imprint","IMPRINT",EDGE,{"derivedFrom":sQuery(id+"F2.wireOp",EDGE,"E26.4.1")}),1.0]])]});
            var Q34;
            Q34=makeQuery(id+"F2.imprint","IMPRINT",FACE,{"disambiguationData":[TD([[makeQuery(id+"F2.imprint","IMPRINT",EDGE,{"derivedFrom":sQuery(id+"F2.wireOp",EDGE,"E26.5.1")}),1.0]])]});
            var Q35;
            Q35=makeQuery(id+"F2.imprint","IMPRINT",FACE,{"disambiguationData":[TD([[makeQuery(id+"F2.imprint","IMPRINT",EDGE,{"derivedFrom":sQuery(id+"F2.wireOp",EDGE,"E26.6.1")}),1.0]])]});
            var Q36;
            {var subQ0=sQuery(id+"F2.wireOp",EDGE,"E23");Q36=makeQuery(id+"F2.imprint","IMPRINT",FACE,{"disambiguationData":[TD([[makeQuery(id+"F2.imprint","IMPRINT",EDGE,{"derivedFrom":subQ0}),1.0]])]});}
            var Q37;
            {var subQ0=sQuery(id+"F2.wireOp",EDGE,"E22");Q37=makeQuery(id+"F2.imprint","IMPRINT",FACE,{"disambiguationData":[TD([[makeQuery(id+"F2.imprint","IMPRINT",EDGE,{"derivedFrom":subQ0}),-1.0]])]});}
            var Q38;
            Q38=makeQuery(id+"F2.imprint","IMPRINT",FACE,{"disambiguationData":[TD([[makeQuery(id+"F2.imprint","IMPRINT",EDGE,{"derivedFrom":sQuery(id+"F2.wireOp",EDGE,"E26.1.1")}),1.0]])]});
            var Q39;
            Q39=makeQuery(id+"F2.imprint","IMPRINT",FACE,{"disambiguationData":[TD([[makeQuery(id+"F2.imprint","IMPRINT",EDGE,{"derivedFrom":sQuery(id+"F2.wireOp",EDGE,"E26.2.1")}),1.0]])]});
            extrude(context, id + "F5", {"entities" : qUnion([Q0, Q1, Q2, Q3, Q4, Q5, Q6, Q7, Q8, Q9, Q10, Q11, Q12, Q13, Q14, Q15, Q16, Q17, Q18, Q19, Q20, Q21, Q22, Q23, Q24, Q25, Q26, Q27, Q28, Q29, Q30, Q31, Q32, Q33, Q34, Q35, Q36, Q37, Q38, Q39]), "operationType" : NewBodyOperationType.REMOVE, "depth" : 25.4 * mm});
        }
        {
            var Q0;
            Q0=qCreatedBy(makeId("Top.planeOp"),FACE);
            var sketch = newSketch(context, id + "F6", { "sketchPlane" : qUnion([Q0])});
            skPoint(sketch, "E174.0", {"position": v(-0.13, -127) * mm});
            skPoint(sketch, "E175.0", {"position": v(0.13, -127) * mm});
            skPoint(sketch, "E176.0", {"position": v(0.13, -126.75) * mm});
            skPoint(sketch, "E177.0", {"position": v(-0.13, -126.75) * mm});
            skPoint(sketch, "E178.0", {"position": v(-0.13, -101.6) * mm});
            skPoint(sketch, "E179.0", {"position": v(0.13, -101.6) * mm});
            skPoint(sketch, "E180.0", {"position": v(0.13, -101.35) * mm});
            skPoint(sketch, "E181.0", {"position": v(-0.13, -101.35) * mm});
            skPoint(sketch, "E182.0", {"position": v(-0.13, -50.55) * mm});
            skPoint(sketch, "E183.0", {"position": v(-0.13, -50.8) * mm});
            skPoint(sketch, "E184.0", {"position": v(0.13, -50.55) * mm});
            skPoint(sketch, "E185.0", {"position": v(0.13, -50.8) * mm});
            skPoint(sketch, "E186.0", {"position": v(-0.13, -25.15) * mm});
            skPoint(sketch, "E187.0", {"position": v(-0.13, -25.4) * mm});
            skPoint(sketch, "E188.0", {"position": v(0.13, -25.4) * mm});
            skPoint(sketch, "E189.0", {"position": v(0.13, -25.15) * mm});
            skPoint(sketch, "E190.0", {"position": v(-0.13, -76.2) * mm});
            skPoint(sketch, "E191.0", {"position": v(0.13, -76.2) * mm});
            skPoint(sketch, "E192.0", {"position": v(0.13, -75.95) * mm});
            skPoint(sketch, "E193.0", {"position": v(-0.13, -75.95) * mm});
            skCircle(sketch, "E194", {"center": v(0, -126.87) * mm, "radius": 0.13 * mm});
            skLineSegment(sketch, "E195", {"start": v(-0.13, -127) * mm, "end": v(-0.13, -126.75) * mm});
            skLineSegment(sketch, "E196", {"start": v(0.13, -127) * mm, "end": v(0.13, -126.75) * mm});
            skLineSegment(sketch, "E197", {"start": v(-0.13, -101.6) * mm, "end": v(-0.13, -101.35) * mm});
            skLineSegment(sketch, "E198", {"start": v(0.13, -101.35) * mm, "end": v(0, -101.35) * mm});
            skCircle(sketch, "E199", {"center": v(0, -101.47) * mm, "radius": 0.13 * mm});
            skPoint(sketch, "E199.centerSnap0", {"position": v(0, -101.35) * mm});
            skPoint(sketch, "E199.centerSnap1", {"position": v(-0.13, -101.47) * mm});
            skLineSegment(sketch, "E200", {"start": v(-0.13, -76.2) * mm, "end": v(-0.13, -76.07) * mm});
            skLineSegment(sketch, "E201", {"start": v(0.13, -75.95) * mm, "end": v(-0.13, -75.95) * mm});
            skCircle(sketch, "E202", {"center": v(0, -76.07) * mm, "radius": 0.13 * mm});
            skPoint(sketch, "E202.centerSnap0", {"position": v(-0.13, -76.07) * mm});
            skPoint(sketch, "E202.centerSnap1", {"position": v(0, -75.95) * mm});
            skLineSegment(sketch, "E203", {"start": v(-0.13, -50.8) * mm, "end": v(-0.13, -50.67) * mm});
            skLineSegment(sketch, "E204", {"start": v(0.13, -50.55) * mm, "end": v(0, -50.55) * mm});
            skCircle(sketch, "E205", {"center": v(0, -50.67) * mm, "radius": 0.13 * mm});
            skPoint(sketch, "E205.centerSnap0", {"position": v(0, -50.55) * mm});
            skPoint(sketch, "E205.centerSnap1", {"position": v(-0.13, -50.67) * mm});
            skLineSegment(sketch, "E206", {"start": v(-0.13, -25.4) * mm, "end": v(-0.13, -25.27) * mm});
            skLineSegment(sketch, "E207", {"start": v(0.13, -25.15) * mm, "end": v(0, -25.15) * mm});
            skCircle(sketch, "E208", {"center": v(0, -25.27) * mm, "radius": 0.13 * mm});
            skPoint(sketch, "E208.centerSnap0", {"position": v(0, -25.15) * mm});
            skPoint(sketch, "E208.centerSnap1", {"position": v(-0.13, -25.27) * mm});
            skCircle(sketch, "E209.1.0", {"center": v(17.87, -17.87) * mm, "radius": 0.13 * mm});
            skCircle(sketch, "E209.1.1", {"center": v(35.83, -35.83) * mm, "radius": 0.13 * mm});
            skCircle(sketch, "E209.1.2", {"center": v(53.8, -53.8) * mm, "radius": 0.13 * mm});
            skCircle(sketch, "E209.1.3", {"center": v(71.75, -71.75) * mm, "radius": 0.13 * mm});
            skCircle(sketch, "E209.1.4", {"center": v(89.71, -89.71) * mm, "radius": 0.13 * mm});
            skCircle(sketch, "E209.2.0", {"center": v(25.27, 0) * mm, "radius": 0.13 * mm});
            skCircle(sketch, "E209.2.1", {"center": v(50.67, 0) * mm, "radius": 0.13 * mm});
            skCircle(sketch, "E209.2.2", {"center": v(76.07, 0) * mm, "radius": 0.13 * mm});
            skCircle(sketch, "E209.2.3", {"center": v(101.47, 0) * mm, "radius": 0.13 * mm});
            skCircle(sketch, "E209.2.4", {"center": v(126.87, 0) * mm, "radius": 0.13 * mm});
            skCircle(sketch, "E209.3.0", {"center": v(17.87, 17.87) * mm, "radius": 0.13 * mm});
            skCircle(sketch, "E209.3.1", {"center": v(35.83, 35.83) * mm, "radius": 0.13 * mm});
            skCircle(sketch, "E209.3.2", {"center": v(53.8, 53.8) * mm, "radius": 0.13 * mm});
            skCircle(sketch, "E209.3.3", {"center": v(71.75, 71.75) * mm, "radius": 0.13 * mm});
            skCircle(sketch, "E209.3.4", {"center": v(89.71, 89.71) * mm, "radius": 0.13 * mm});
            skCircle(sketch, "E209.4.0", {"center": v(0, 25.27) * mm, "radius": 0.13 * mm});
            skCircle(sketch, "E209.4.1", {"center": v(0, 50.67) * mm, "radius": 0.13 * mm});
            skCircle(sketch, "E209.4.2", {"center": v(0, 76.07) * mm, "radius": 0.13 * mm});
            skCircle(sketch, "E209.4.3", {"center": v(0, 101.47) * mm, "radius": 0.13 * mm});
            skCircle(sketch, "E209.4.4", {"center": v(0, 126.87) * mm, "radius": 0.13 * mm});
            skCircle(sketch, "E209.5.0", {"center": v(-17.87, 17.87) * mm, "radius": 0.13 * mm});
            skCircle(sketch, "E209.5.1", {"center": v(-35.83, 35.83) * mm, "radius": 0.13 * mm});
            skCircle(sketch, "E209.5.2", {"center": v(-53.8, 53.8) * mm, "radius": 0.13 * mm});
            skCircle(sketch, "E209.5.3", {"center": v(-71.75, 71.75) * mm, "radius": 0.13 * mm});
            skCircle(sketch, "E209.5.4", {"center": v(-89.71, 89.71) * mm, "radius": 0.13 * mm});
            skCircle(sketch, "E209.6.0", {"center": v(-25.27, 0) * mm, "radius": 0.13 * mm});
            skCircle(sketch, "E209.6.1", {"center": v(-50.67, 0) * mm, "radius": 0.13 * mm});
            skCircle(sketch, "E209.6.2", {"center": v(-76.07, 0) * mm, "radius": 0.13 * mm});
            skCircle(sketch, "E209.6.3", {"center": v(-101.47, 0) * mm, "radius": 0.13 * mm});
            skCircle(sketch, "E209.6.4", {"center": v(-126.87, 0) * mm, "radius": 0.13 * mm});
            skCircle(sketch, "E209.7.0", {"center": v(-17.87, -17.87) * mm, "radius": 0.13 * mm});
            skCircle(sketch, "E209.7.1", {"center": v(-35.83, -35.83) * mm, "radius": 0.13 * mm});
            skCircle(sketch, "E209.7.2", {"center": v(-53.8, -53.8) * mm, "radius": 0.13 * mm});
            skCircle(sketch, "E209.7.3", {"center": v(-71.75, -71.75) * mm, "radius": 0.13 * mm});
            skCircle(sketch, "E209.7.4", {"center": v(-89.71, -89.71) * mm, "radius": 0.13 * mm});
            skPoint(sketch, "E209.center", {"position": v(0, 0) * mm});
            skSolve(sketch);
        }
        {
            var Q0;
            Q0 = qSketchRegion(id + "F6", true);
            extrude(context, id + "F7", {"entities" : qUnion([Q0]), "operationType" : NewBodyOperationType.ADD, "depth" : 0.81 * mm});
        }
        {
            var Q0;
            Q0=qCreatedBy(makeId("Top.planeOp"),FACE);
            var sketch = newSketch(context, id + "F8", { "sketchPlane" : qUnion([Q0])});
            skCircle(sketch, "E210", {"center": v(0, 0) * mm, "radius": 127 * mm});
            skArc(sketch, "E211.0", {"start": v(-0.13, -4.44) * mm, "mid": v(-1.7, -4.1) * mm, "end": v(-3.05, -3.23) * mm});
            skArc(sketch, "E212.0", {"start": v(-3.23, -3.05) * mm, "mid": v(-4.1, -1.7) * mm, "end": v(-4.44, -0.13) * mm});
            skArc(sketch, "E213.0", {"start": v(-4.44, 0.13) * mm, "mid": v(-4.1, 1.7) * mm, "end": v(-3.23, 3.05) * mm});
            skArc(sketch, "E214.0", {"start": v(-3.05, 3.23) * mm, "mid": v(-1.7, 4.1) * mm, "end": v(-0.13, 4.44) * mm});
            skArc(sketch, "E215.0", {"start": v(0.13, 4.44) * mm, "mid": v(1.7, 4.1) * mm, "end": v(3.05, 3.23) * mm});
            skArc(sketch, "E216.0", {"start": v(3.23, 3.05) * mm, "mid": v(4.1, 1.7) * mm, "end": v(4.44, 0.13) * mm});
            skArc(sketch, "E217.0", {"start": v(4.44, -0.13) * mm, "mid": v(4.1, -1.7) * mm, "end": v(3.23, -3.05) * mm});
            skArc(sketch, "E218.0", {"start": v(3.05, -3.23) * mm, "mid": v(1.7, -4.1) * mm, "end": v(0.13, -4.44) * mm});
            skArc(sketch, "E219.0", {"start": v(0.13, -4.44) * mm, "mid": v(0, -4.45) * mm, "end": v(-0.13, -4.44) * mm});
            skArc(sketch, "E220.0", {"start": v(-3.05, -3.23) * mm, "mid": v(-3.14, -3.14) * mm, "end": v(-3.23, -3.05) * mm});
            skArc(sketch, "E221.0", {"start": v(3.23, -3.05) * mm, "mid": v(3.14, -3.14) * mm, "end": v(3.05, -3.23) * mm});
            skArc(sketch, "E222.0", {"start": v(-4.44, -0.13) * mm, "mid": v(-4.44, 0) * mm, "end": v(-4.44, 0.13) * mm});
            skArc(sketch, "E223.0", {"start": v(4.44, 0.13) * mm, "mid": v(4.45, 0) * mm, "end": v(4.44, -0.13) * mm});
            skArc(sketch, "E224.0", {"start": v(-3.23, 3.05) * mm, "mid": v(-3.14, 3.14) * mm, "end": v(-3.05, 3.23) * mm});
            skArc(sketch, "E225.0", {"start": v(-0.13, 4.44) * mm, "mid": v(0, 4.45) * mm, "end": v(0.13, 4.44) * mm});
            skArc(sketch, "E226.0", {"start": v(3.05, 3.23) * mm, "mid": v(3.14, 3.14) * mm, "end": v(3.23, 3.05) * mm});
            skSolve(sketch);
        }
        {
            var Q0;
            Q0 = qSketchRegion(id + "F8", true);
            extrude(context, id + "F9", {"entities" : qUnion([Q0]), "oppositeDirection" : true, "depth" : 0.25 * mm});
        }
    });
